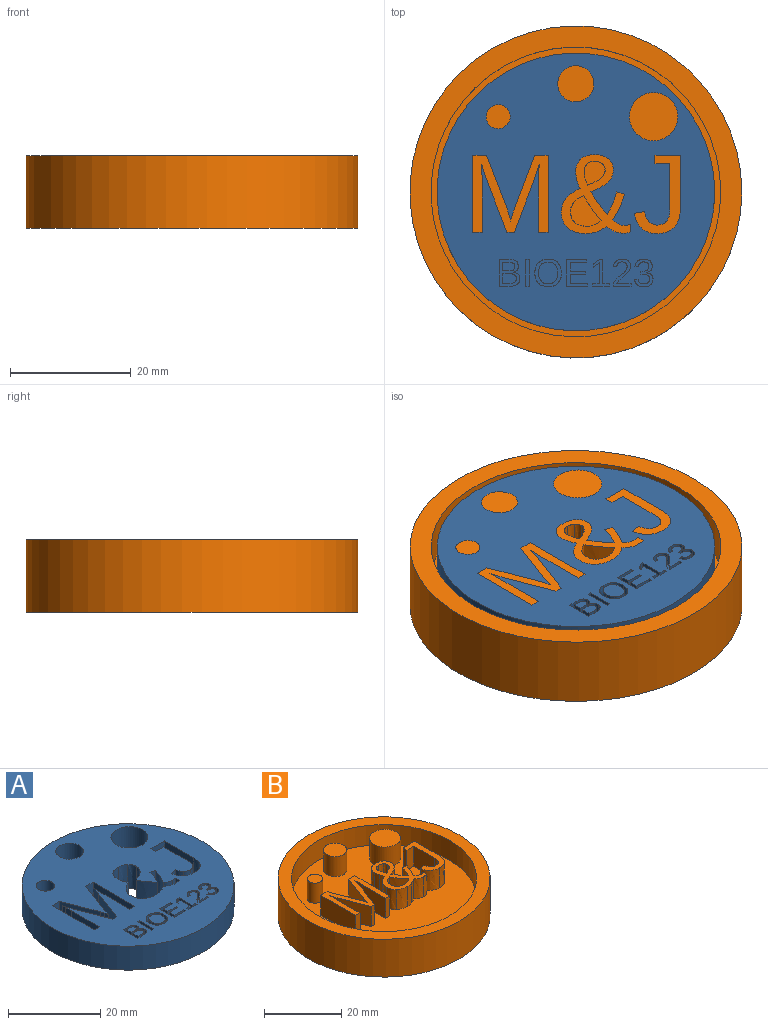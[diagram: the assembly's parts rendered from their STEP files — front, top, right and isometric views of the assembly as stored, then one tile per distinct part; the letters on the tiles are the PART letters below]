
ASSEMBLY  parts=2 mates=1
PART A: 196 faces, bbox 46x46x6.4 mm
  f0: plane 46x46mm, normal (0,0,1), area 1324.2mm2, adj f1,f2,f3,f4,f5,f6,f7,f8
  f1: plane 6.35x1.56mm, normal (0,1,0), area 9.9mm2, adj f0,f2,f62,f63
  f2: plane 8.56x6.35mm, normal (1,0,0), area 54.4mm2, adj f0,f1,f3,f63
  f3: extruded ~6.35x2.73mm, area 17.3mm2, adj f0,f2,f4,f63
  f4: extruded ~6.35x2.55mm, area 17mm2, adj f0,f3,f5,f63
  f5: plane 8.74x6.35mm, normal (-0.93,0.35,0), area 59.4mm2, adj f0,f4,f6,f63
  f6: plane 6.35x1.22mm, normal (0,1,0), area 7.7mm2, adj f0,f5,f7,f63
  f7: plane 8.74x6.35mm, normal (0.93,0.36,0), area 59.5mm2, adj f0,f6,f8,f63
  f8: plane 6.35x1.55mm, normal (0.95,0.31,0), area 10.3mm2, adj f0,f7,f9,f63
  f9: plane 6.35x1mm, normal (0.96,0.29,0), area 6.6mm2, adj f0,f8,f10,f63
  f10: plane 6.35x1.01mm, normal (-1,-0.03,0), area 6.4mm2, adj f0,f9,f11,f63
  f11: plane 6.35x1.72mm, normal (-1,-0.02,0), area 10.9mm2, adj f0,f10,f12,f63
  f12: plane 8.56x6.35mm, normal (-1,0,0), area 54.4mm2, adj f0,f11,f13,f63
  f13: plane 6.35x1.55mm, normal (0,1,0), area 9.8mm2, adj f0,f12,f14,f63
  f14: plane 12.83x6.35mm, normal (1,0,0), area 81.5mm2, adj f0,f13,f15,f63
  f15: plane 6.35x2.28mm, normal (0,-1,0), area 14.5mm2, adj f0,f14,f16,f63
  f16: plane 8.9x6.35mm, normal (-0.93,-0.36,0), area 60.5mm2, adj f0,f15,f17,f63
  f17: extruded ~6.35x1.15mm, area 7.6mm2, adj f0,f16,f18,f63
  f18: extruded ~6.35x0.89mm, area 5.8mm2, adj f0,f17,f19,f63
  f19: extruded ~6.35x1.11mm, area 7.3mm2, adj f0,f18,f20,f63
  f20: extruded ~6.35x0.93mm, area 6.3mm2, adj f0,f19,f21,f63
  f21: plane 8.9x6.35mm, normal (0.94,-0.35,0), area 60.4mm2, adj f0,f20,f22,f63
  f22: plane 6.35x2.23mm, normal (0,-1,0), area 14.2mm2, adj f0,f21,f62,f63
  f23: extruded ~6.35x1.29mm, area 8.3mm2, adj f0,f24,f56,f63
  f24: extruded ~6.35x2.71mm, area 19.3mm2, adj f0,f23,f25,f63
  f25: extruded ~6.35x1.56mm, area 11.5mm2, adj f0,f24,f26,f63
  f26: extruded ~6.35x1.83mm, area 11.9mm2, adj f0,f25,f27,f63
  f27: extruded ~6.35x3.03mm, area 20.6mm2, adj f0,f26,f28,f63
  f28: extruded ~6.35x2.62mm, area 18.6mm2, adj f0,f27,f29,f63
  f29: extruded ~6.35x3.91mm, area 33.8mm2, adj f0,f28,f30,f63
  f30: extruded ~6.35x1.34mm, area 9.1mm2, adj f0,f29,f31,f63
  f31: extruded ~6.35x1.41mm, area 9.1mm2, adj f0,f30,f32,f63
  f32: extruded ~6.35x2.12mm, area 14.9mm2, adj f0,f31,f33,f63
  f33: extruded ~6.35x2.36mm, area 16.1mm2, adj f0,f32,f34,f63
  f34: extruded ~6.35x2.22mm, area 15.1mm2, adj f0,f33,f35,f63
  f35: extruded ~6.35x1.89mm, area 13.6mm2, adj f0,f34,f36,f63
  f36: extruded ~6.35x1.91mm, area 13.6mm2, adj f0,f35,f37,f63
  f37: extruded ~6.35x2.89mm, area 21.3mm2, adj f0,f36,f38,f63
  f38: extruded ~6.35x3.75mm, area 29.3mm2, adj f0,f37,f39,f63
  f39: extruded ~6.35x3.73mm, area 25.8mm2, adj f0,f38,f40,f63
  f40: plane 6.35x1.32mm, normal (-0.28,-0.96,0), area 8.7mm2, adj f0,f39,f41,f63
  f41: extruded ~6.35x4.27mm, area 29.9mm2, adj f0,f40,f42,f63
  f42: extruded ~6.35x1.89mm, area 13.7mm2, adj f0,f41,f43,f63
  f43: extruded ~6.35x1.07mm, area 6.9mm2, adj f0,f42,f56,f63
  f44: extruded ~6.35x2.77mm, area 19.4mm2, adj f0,f45,f61,f63
  f45: extruded ~6.35x3.87mm, area 36.1mm2, adj f0,f44,f46,f63
  f46: plane 6.35x1.7mm, normal (0.16,-0.99,0), area 11mm2, adj f0,f45,f47,f63
  f47: extruded ~6.35x1.65mm, area 11.7mm2, adj f0,f46,f48,f63
  f48: extruded ~6.35x1.44mm, area 10.2mm2, adj f0,f47,f49,f63
  f49: extruded ~6.35x1.49mm, area 10.7mm2, adj f0,f48,f50,f63
  f50: extruded ~6.35x1.91mm, area 12.9mm2, adj f0,f49,f51,f63
  f51: plane 7.62x6.35mm, normal (1,0,0), area 48.4mm2, adj f0,f50,f52,f63
  f52: plane 6.35x2.47mm, normal (0,1,0), area 15.7mm2, adj f0,f51,f53,f63
  f53: plane 6.35x1.42mm, normal (1,0,0), area 9mm2, adj f0,f52,f54,f63
  f54: plane 6.35x4.2mm, normal (0,-1,0), area 26.7mm2, adj f0,f53,f55,f63
  f55: plane 9x6.35mm, normal (-1,0,0), area 57.2mm2, adj f0,f54,f61,f63
  f56: plane 6.35x1.23mm, normal (-1,0,0), area 7.8mm2, adj f0,f23,f43,f63
  f57: cylinder r=3mm len=6.35mm, axis (0,0,-1), area 119.7mm2, adj f0,f63
  f58: cylinder r=4mm len=8mm, axis (0,0,-1), area 159.6mm2, adj f0,f63
  f59: cylinder r=2mm len=6.35mm, axis (0,0,-1), area 79.8mm2, adj f0,f63
  f60: cylinder r=23mm len=46mm, axis (0,0,-1), area 917.7mm2, adj f0,f63
  f61: extruded ~6.35x2.94mm, area 20.2mm2, adj f0,f44,f55,f63
  f62: plane 12.83x6.35mm, normal (-1,0,0), area 81.5mm2, adj f0,f1,f22,f63
  f63: plane 46x46mm, normal (0,0,-1), area 1378.5mm2, adj f1,f2,f3,f4,f5,f6,f7,f8
  f64: plane 4.46x2mm, normal (1,0,0), area 8.9mm2, adj f0,f65,f67,f68
  f65: plane 2x0.6mm, normal (0,1,0), area 1.2mm2, adj f0,f64,f66,f68
  f66: plane 4.46x2mm, normal (-1,0,0), area 8.9mm2, adj f0,f65,f67,f68
  f67: plane 2x0.6mm, normal (0,-1,0), area 1.2mm2, adj f0,f64,f66,f68
  f68: plane 4.46x0.6mm, normal (0,0,1), area 2.7mm2, adj f64,f65,f66,f67
  f69: plane 4.46x2mm, normal (1,0,0), area 8.9mm2, adj f0,f70,f80,f81
  f70: plane 3.51x2mm, normal (0,1,0), area 7mm2, adj f0,f69,f71,f81
  f71: plane 2x0.49mm, normal (-1,0,0), area 1mm2, adj f0,f70,f72,f81
  f72: plane 2.91x2mm, normal (0,-1,0), area 5.8mm2, adj f0,f71,f73,f81
  f73: plane 2x1.55mm, normal (-1,0,0), area 3.1mm2, adj f0,f72,f74,f81
  f74: plane 2.59x2mm, normal (0,1,0), area 5.2mm2, adj f0,f73,f75,f81
  f75: plane 2x0.49mm, normal (-1,0,0), area 1mm2, adj f0,f74,f76,f81
  f76: plane 2.59x2mm, normal (0,-1,0), area 5.2mm2, adj f0,f75,f77,f81
  f77: plane 2x1.43mm, normal (-1,0,0), area 2.9mm2, adj f0,f76,f78,f81
  f78: plane 2.78x2mm, normal (0,1,0), area 5.6mm2, adj f0,f77,f79,f81
  f79: plane 2x0.49mm, normal (-1,0,0), area 1mm2, adj f0,f78,f80,f81
  f80: plane 3.38x2mm, normal (0,-1,0), area 6.8mm2, adj f0,f69,f79,f81
  f81: plane 4.46x3.51mm, normal (0,0,1), area 6.8mm2, adj f69,f70,f71,f72,f73,f74,f75,f76
  f82: plane 2x0.48mm, normal (1,0,0), area 1mm2, adj f0,f83,f92,f93
  f83: plane 2.79x2mm, normal (0,1,0), area 5.6mm2, adj f0,f82,f84,f93
  f84: plane 2x0.48mm, normal (-1,0,0), area 1mm2, adj f0,f83,f85,f93
  f85: plane 2x1.09mm, normal (0,-1,0), area 2.2mm2, adj f0,f84,f86,f93
  f86: plane 3.97x2mm, normal (-1,0,0), area 7.9mm2, adj f0,f85,f87,f93
  f87: plane 2x0.53mm, normal (0,-1,0), area 1.1mm2, adj f0,f86,f88,f93
  f88: plane 2x1.05mm, normal (0.57,-0.82,0), area 2.6mm2, adj f0,f87,f89,f93
  f89: plane 2x0.54mm, normal (1,0,0), area 1.1mm2, adj f0,f88,f90,f93
  f90: plane 2x1.01mm, normal (-0.58,0.81,0), area 2.5mm2, adj f0,f89,f91,f93
  f91: plane 3.43x2mm, normal (1,0,0), area 6.9mm2, adj f0,f90,f92,f93
  f92: plane 2x1.14mm, normal (0,-1,0), area 2.3mm2, adj f0,f82,f91,f93
  f93: plane 4.46x2.79mm, normal (0,0,1), area 4.2mm2, adj f82,f83,f84,f85,f86,f87,f88,f89
  f94: plane 2x0.4mm, normal (1,0,0), area 0.8mm2, adj f0,f95,f117,f118
  f95: plane 2.95x2mm, normal (0,1,0), area 5.9mm2, adj f0,f94,f96,f118
  f96: plane 2x0.48mm, normal (-1,0,0), area 1mm2, adj f0,f95,f97,f118
  f97: plane 2.33x2mm, normal (0,-1,0), area 4.7mm2, adj f0,f96,f98,f118
  f98: extruded ~2x0.46mm, area 1.1mm2, adj f0,f97,f99,f118
  f99: extruded ~2x0.58mm, area 1.6mm2, adj f0,f98,f100,f118
  f100: extruded ~2x0.9mm, area 2.4mm2, adj f0,f99,f101,f118
  f101: extruded ~2x0.51mm, area 1.2mm2, adj f0,f100,f102,f118
  f102: extruded ~2x0.52mm, area 1.1mm2, adj f0,f101,f103,f118
  f103: extruded ~2x0.9mm, area 2mm2, adj f0,f102,f104,f118
  f104: extruded ~2x1.04mm, area 2.2mm2, adj f0,f103,f105,f118
  f105: extruded ~2x1.01mm, area 2.2mm2, adj f0,f104,f106,f118
  f106: extruded ~2x0.85mm, area 2mm2, adj f0,f105,f107,f118
  f107: plane 2x0.58mm, normal (0.09,1,0), area 1.2mm2, adj f0,f106,f108,f118
  f108: extruded ~2x0.56mm, area 1.3mm2, adj f0,f107,f109,f118
  f109: extruded ~2x0.6mm, area 1.3mm2, adj f0,f108,f110,f118
  f110: extruded ~2x0.6mm, area 1.3mm2, adj f0,f109,f111,f118
  f111: extruded ~2x0.57mm, area 1.3mm2, adj f0,f110,f112,f118
  f112: extruded ~2x0.49mm, area 1mm2, adj f0,f111,f113,f118
  f113: extruded ~2x0.41mm, area 1.1mm2, adj f0,f112,f114,f118
  f114: extruded ~2x0.45mm, area 1.2mm2, adj f0,f113,f115,f118
  f115: extruded ~2x0.51mm, area 1.3mm2, adj f0,f114,f116,f118
  f116: extruded ~2x0.51mm, area 1.4mm2, adj f0,f115,f117,f118
  f117: extruded ~2x0.65mm, area 1.5mm2, adj f0,f94,f116,f118
  f118: plane 4.53x2.95mm, normal (0,0,1), area 5.1mm2, adj f94,f95,f96,f97,f98,f99,f100,f101
  f119: extruded ~2x0.96mm, area 2.1mm2, adj f0,f120,f147,f148
  f120: extruded ~2x0.71mm, area 1.6mm2, adj f0,f119,f121,f148
  f121: extruded ~2x0.78mm, area 1.7mm2, adj f0,f120,f122,f148
  f122: plane 2x0.01mm, normal (-1,0,0), area 0mm2, adj f0,f121,f123,f148
  f123: extruded ~2x0.69mm, area 1.6mm2, adj f0,f122,f124,f148
  f124: extruded ~2x0.69mm, area 1.5mm2, adj f0,f123,f125,f148
  f125: extruded ~2x0.87mm, area 2mm2, adj f0,f124,f126,f148
  f126: extruded ~2x1.04mm, area 2.2mm2, adj f0,f125,f127,f148
  f127: extruded ~2x1mm, area 2.1mm2, adj f0,f126,f128,f148
  f128: extruded ~2x0.85mm, area 2mm2, adj f0,f127,f129,f148
  f129: plane 2x0.57mm, normal (0.08,1,0), area 1.1mm2, adj f0,f128,f130,f148
  f130: extruded ~2x0.54mm, area 1.2mm2, adj f0,f129,f131,f148
  f131: extruded ~2x0.61mm, area 1.3mm2, adj f0,f130,f132,f148
  f132: extruded ~2x0.63mm, area 1.4mm2, adj f0,f131,f133,f148
  f133: extruded ~2x0.56mm, area 1.2mm2, adj f0,f132,f134,f148
  f134: extruded ~2x0.57mm, area 1.3mm2, adj f0,f133,f135,f148
  f135: extruded ~2x0.73mm, area 1.5mm2, adj f0,f134,f136,f148
  f136: plane 2x0.31mm, normal (0,-1,0), area 0.6mm2, adj f0,f135,f137,f148
  f137: plane 2x0.49mm, normal (1,0,0), area 1mm2, adj f0,f136,f138,f148
  f138: plane 2x0.32mm, normal (0,1,0), area 0.6mm2, adj f0,f137,f139,f148
  f139: extruded ~2x0.81mm, area 1.7mm2, adj f0,f138,f140,f148
  f140: extruded ~2x0.57mm, area 1.3mm2, adj f0,f139,f141,f148
  f141: extruded ~2x0.63mm, area 1.4mm2, adj f0,f140,f142,f148
  f142: extruded ~2x0.68mm, area 1.4mm2, adj f0,f141,f143,f148
  f143: extruded ~2x0.97mm, area 2.8mm2, adj f0,f142,f144,f148
  f144: plane 2x0.59mm, normal (0.09,-1,0), area 1.2mm2, adj f0,f143,f145,f148
  f145: extruded ~2x0.9mm, area 2.1mm2, adj f0,f144,f146,f148
  f146: extruded ~2x1.08mm, area 2.3mm2, adj f0,f145,f147,f148
  f147: extruded ~2x1.12mm, area 2.4mm2, adj f0,f119,f146,f148
  f148: plane 4.59x3.07mm, normal (0,0,1), area 5.4mm2, adj f119,f120,f121,f122,f123,f124,f125,f126
  f149: extruded ~2x1.31mm, area 2.8mm2, adj f150,f167,f168,f194
  f150: extruded ~2x1.35mm, area 2.9mm2, adj f149,f151,f168,f194
  f151: extruded ~2x1.19mm, area 2.6mm2, adj f150,f152,f168,f194
  f152: extruded ~2x1.17mm, area 2.6mm2, adj f151,f153,f168,f194
  f153: extruded ~2x1.33mm, area 2.9mm2, adj f152,f154,f168,f194
  f154: extruded ~2x1.31mm, area 2.8mm2, adj f153,f155,f168,f194
  f155: extruded ~2x1.18mm, area 2.6mm2, adj f154,f167,f168,f194
  f156: extruded ~2x1.22mm, area 2.5mm2, adj f0,f157,f166,f168
  f157: extruded ~2x1.22mm, area 2.5mm2, adj f0,f156,f158,f168
  f158: extruded ~2x0.79mm, area 2.2mm2, adj f0,f157,f159,f168
  f159: extruded ~2x1.18mm, area 2.4mm2, adj f0,f158,f160,f168
  f160: extruded ~2x1.63mm, area 3.6mm2, adj f0,f159,f161,f168
  f161: extruded ~2x1.67mm, area 3.6mm2, adj f0,f160,f162,f168
  f162: extruded ~2x1.23mm, area 2.5mm2, adj f0,f161,f163,f168
  f163: extruded ~2x0.81mm, area 2.3mm2, adj f0,f162,f164,f168
  f164: extruded ~2x1.18mm, area 2.5mm2, adj f0,f163,f165,f168
  f165: extruded ~2x1.18mm, area 2.5mm2, adj f0,f164,f166,f168
  f166: extruded ~2x0.81mm, area 2.3mm2, adj f0,f156,f165,f168
  f167: extruded ~2x1.18mm, area 2.6mm2, adj f149,f155,f168,f194
  f168: plane 4.59x4.42mm, normal (0,0,1), area 7.1mm2, adj f149,f150,f151,f152,f153,f154,f155,f156
  f169: extruded ~2x1.11mm, area 3.1mm2, adj f170,f191,f192,f195
  f170: extruded ~2x0.61mm, area 1.4mm2, adj f169,f171,f192,f195
  f171: extruded ~2x0.81mm, area 1.7mm2, adj f170,f172,f192,f195
  f172: plane 2x1.17mm, normal (0,-1,0), area 2.3mm2, adj f171,f173,f192,f195
  f173: plane 2x1.61mm, normal (-1,0,0), area 3.2mm2, adj f172,f191,f192,f195
  f174: extruded ~2x0.52mm, area 1.2mm2, adj f175,f189,f192,f193
  f175: extruded ~2x0.56mm, area 1.3mm2, adj f174,f176,f192,f193
  f176: extruded ~2x0.72mm, area 1.5mm2, adj f175,f177,f192,f193
  f177: plane 2x1.02mm, normal (0,-1,0), area 2mm2, adj f176,f178,f192,f193
  f178: plane 2x1.41mm, normal (-1,0,0), area 2.8mm2, adj f177,f179,f192,f193
  f179: plane 2x1.02mm, normal (0,1,0), area 2mm2, adj f178,f189,f192,f193
  f180: extruded ~2x0.93mm, area 2.1mm2, adj f0,f181,f190,f192
  f181: extruded ~2x0.74mm, area 1.6mm2, adj f0,f180,f182,f192
  f182: extruded ~2x0.82mm, area 1.8mm2, adj f0,f181,f183,f192
  f183: extruded ~2x0.63mm, area 1.5mm2, adj f0,f182,f184,f192
  f184: extruded ~2x0.66mm, area 1.4mm2, adj f0,f183,f185,f192
  f185: extruded ~2x1.57mm, area 4.3mm2, adj f0,f184,f186,f192
  f186: plane 2x1.62mm, normal (0,-1,0), area 3.2mm2, adj f0,f185,f187,f192
  f187: plane 4.46x2mm, normal (1,0,0), area 8.9mm2, adj f0,f186,f188,f192
  f188: plane 2x1.81mm, normal (0,1,0), area 3.6mm2, adj f0,f187,f190,f192
  f189: extruded ~2x0.72mm, area 1.5mm2, adj f174,f179,f192,f193
  f190: extruded ~2x1.21mm, area 2.5mm2, adj f0,f180,f188,f192
  f191: plane 2x1.13mm, normal (0,1,0), area 2.3mm2, adj f169,f173,f192,f195
  f192: plane 4.46x3.45mm, normal (0,0,1), area 7.8mm2, adj f169,f170,f171,f172,f173,f174,f175,f176
  f193: plane 1.98x1.41mm, normal (0,0,1), area 2.6mm2, adj f174,f175,f176,f177,f178,f179,f189
  f194: plane 3.6x3.19mm, normal (0,0,1), area 9.4mm2, adj f149,f150,f151,f152,f153,f154,f155,f167
  f195: plane 2.23x1.61mm, normal (0,0,1), area 3.3mm2, adj f169,f170,f171,f172,f173,f191
PART B: 88 faces, bbox 55x55x12 mm
  f0: plane 48x48mm, normal (0,0,1), area 1526.2mm2, adj f4,f6,f7,f8,f9,f10,f11,f12
  f1: cylinder r=27.5mm len=55mm, axis (0,0,-1), area 2073.5mm2, adj f2,f3
  f2: plane 55x55mm, normal (0,0,1), area 566.3mm2, adj f1,f4
  f3: plane 55x55mm, normal (0,0,-1), area 2375.8mm2, adj f1
  f4: cylinder r=24mm len=48mm, axis (0,0,1), area 957.6mm2, adj f0,f2
  f5: plane 12.83x12.47mm, normal (0,0,1), area 74.4mm2, adj f6,f7,f8,f9,f10,f11,f12,f13
  f6: plane 6.35x1.56mm, normal (0,-1,0), area 9.9mm2, adj f0,f5,f7,f27
  f7: plane 12.83x6.35mm, normal (1,0,0), area 81.5mm2, adj f0,f5,f6,f8
  f8: plane 6.35x2.23mm, normal (0,1,0), area 14.2mm2, adj f0,f5,f7,f9
  f9: plane 8.9x6.35mm, normal (-0.94,0.35,0), area 60.4mm2, adj f0,f5,f8,f10
  f10: extruded ~6.35x0.93mm, area 6.3mm2, adj f0,f5,f9,f11
  f11: extruded ~6.35x1.11mm, area 7.3mm2, adj f0,f5,f10,f12
  f12: extruded ~6.35x0.89mm, area 5.8mm2, adj f0,f5,f11,f13
  f13: extruded ~6.35x1.15mm, area 7.6mm2, adj f0,f5,f12,f14
  f14: plane 8.9x6.35mm, normal (0.93,0.36,0), area 60.5mm2, adj f0,f5,f13,f15
  f15: plane 6.35x2.28mm, normal (0,1,0), area 14.5mm2, adj f0,f5,f14,f16
  f16: plane 12.83x6.35mm, normal (-1,0,0), area 81.5mm2, adj f0,f5,f15,f17
  f17: plane 6.35x1.55mm, normal (0,-1,0), area 9.8mm2, adj f0,f5,f16,f18
  f18: plane 8.56x6.35mm, normal (1,0,0), area 54.4mm2, adj f0,f5,f17,f19
  f19: plane 6.35x1.72mm, normal (1,0.02,0), area 10.9mm2, adj f0,f5,f18,f20
  f20: plane 6.35x1.01mm, normal (1,0.03,0), area 6.4mm2, adj f0,f5,f19,f21
  f21: plane 6.35x1mm, normal (-0.96,-0.29,0), area 6.6mm2, adj f0,f5,f20,f22
  f22: plane 6.35x1.55mm, normal (-0.95,-0.31,0), area 10.3mm2, adj f0,f5,f21,f23
  f23: plane 8.74x6.35mm, normal (-0.93,-0.36,0), area 59.5mm2, adj f0,f5,f22,f24
  f24: plane 6.35x1.22mm, normal (0,-1,0), area 7.7mm2, adj f0,f5,f23,f25
  f25: plane 8.74x6.35mm, normal (0.93,-0.35,0), area 59.4mm2, adj f0,f5,f24,f26
  f26: extruded ~6.35x2.55mm, area 17mm2, adj f0,f5,f25,f28
  f27: plane 8.56x6.35mm, normal (-1,0,0), area 54.4mm2, adj f0,f5,f6,f28
  f28: extruded ~6.35x2.73mm, area 17.3mm2, adj f0,f5,f26,f27
  f29: plane 13.09x11.49mm, normal (0,0,1), area 57.4mm2, adj f30,f31,f32,f33,f34,f35,f36,f37
  f30: extruded ~6.35x1.13mm, area 8.5mm2, adj f29,f31,f58,f67
  f31: extruded ~6.35x1.29mm, area 8.4mm2, adj f29,f30,f32,f67
  f32: extruded ~6.35x1.93mm, area 13.2mm2, adj f29,f31,f57,f67
  f33: extruded ~6.35x0.9mm, area 6.1mm2, adj f29,f34,f64,f66
  f34: extruded ~6.35x0.85mm, area 7.3mm2, adj f29,f33,f35,f66
  f35: extruded ~6.35x1.75mm, area 12.4mm2, adj f29,f34,f36,f66
  f36: extruded ~6.35x2.22mm, area 14.7mm2, adj f29,f35,f37,f66
  f37: extruded ~6.35x1.3mm, area 9mm2, adj f29,f36,f63,f66
  f38: extruded ~6.35x1.29mm, area 8.3mm2, adj f0,f29,f39,f61
  f39: plane 6.35x1.23mm, normal (1,0,0), area 7.8mm2, adj f0,f29,f38,f40
  f40: extruded ~6.35x1.07mm, area 6.9mm2, adj f0,f29,f39,f41
  f41: extruded ~6.35x1.89mm, area 13.7mm2, adj f0,f29,f40,f42
  f42: extruded ~6.35x4.27mm, area 29.9mm2, adj f0,f29,f41,f43
  f43: plane 6.35x1.32mm, normal (0.28,0.96,0), area 8.7mm2, adj f0,f29,f42,f44
  f44: extruded ~6.35x3.73mm, area 25.8mm2, adj f0,f29,f43,f45
  f45: extruded ~6.35x3.75mm, area 29.3mm2, adj f0,f29,f44,f46
  f46: extruded ~6.35x2.89mm, area 21.3mm2, adj f0,f29,f45,f47
  f47: extruded ~6.35x1.91mm, area 13.6mm2, adj f0,f29,f46,f48
  f48: extruded ~6.35x1.89mm, area 13.6mm2, adj f0,f29,f47,f49
  f49: extruded ~6.35x2.22mm, area 15.1mm2, adj f0,f29,f48,f50
  f50: extruded ~6.35x2.36mm, area 16.1mm2, adj f0,f29,f49,f51
  f51: extruded ~6.35x2.12mm, area 14.9mm2, adj f0,f29,f50,f52
  f52: extruded ~6.35x1.41mm, area 9.1mm2, adj f0,f29,f51,f53
  f53: extruded ~6.35x1.34mm, area 9.1mm2, adj f0,f29,f52,f54
  f54: extruded ~6.35x3.91mm, area 33.8mm2, adj f0,f29,f53,f55
  f55: extruded ~6.35x2.62mm, area 18.6mm2, adj f0,f29,f54,f56
  f56: extruded ~6.35x3.03mm, area 20.6mm2, adj f0,f29,f55,f60
  f57: extruded ~6.35x1.74mm, area 12.3mm2, adj f29,f32,f59,f67
  f58: extruded ~6.35x4.16mm, area 32.3mm2, adj f29,f30,f59,f67
  f59: extruded ~6.35x2.74mm, area 23.6mm2, adj f29,f57,f58,f67
  f60: extruded ~6.35x1.83mm, area 11.9mm2, adj f0,f29,f56,f62
  f61: extruded ~6.35x2.71mm, area 19.3mm2, adj f0,f29,f38,f62
  f62: extruded ~6.35x1.56mm, area 11.5mm2, adj f0,f29,f60,f61
  f63: extruded ~6.35x1.33mm, area 9.2mm2, adj f29,f37,f65,f66
  f64: extruded ~6.35x1.07mm, area 7.6mm2, adj f29,f33,f65,f66
  f65: extruded ~6.35x1.24mm, area 8.5mm2, adj f29,f63,f64,f66
  f66: plane 3.99x3.48mm, normal (0,0,1), area 10.2mm2, adj f33,f34,f35,f36,f37,f63,f64,f65
  f67: plane 5.13x5.05mm, normal (0,0,1), area 15.9mm2, adj f30,f31,f32,f57,f58,f59
  f68: plane 13.01x7.65mm, normal (0,0,1), area 34.4mm2, adj f69,f70,f71,f72,f73,f74,f75,f76
  f69: extruded ~6.35x2.77mm, area 19.4mm2, adj f0,f68,f70,f80
  f70: extruded ~6.35x2.94mm, area 20.2mm2, adj f0,f68,f69,f71
  f71: plane 9x6.35mm, normal (1,0,0), area 57.2mm2, adj f0,f68,f70,f72
  f72: plane 6.35x4.2mm, normal (0,1,0), area 26.7mm2, adj f0,f68,f71,f73
  f73: plane 6.35x1.42mm, normal (-1,0,0), area 9mm2, adj f0,f68,f72,f74
  f74: plane 6.35x2.47mm, normal (0,-1,0), area 15.7mm2, adj f0,f68,f73,f75
  f75: plane 7.62x6.35mm, normal (-1,0,0), area 48.4mm2, adj f0,f68,f74,f76
  f76: extruded ~6.35x1.91mm, area 12.9mm2, adj f0,f68,f75,f77
  f77: extruded ~6.35x1.49mm, area 10.7mm2, adj f0,f68,f76,f78
  f78: extruded ~6.35x1.44mm, area 10.2mm2, adj f0,f68,f77,f79
  f79: extruded ~6.35x1.65mm, area 11.7mm2, adj f0,f68,f78,f81
  f80: extruded ~6.35x3.87mm, area 36.1mm2, adj f0,f68,f69,f81
  f81: plane 6.35x1.7mm, normal (-0.16,0.99,0), area 11mm2, adj f0,f68,f79,f80
  f82: plane 6x6mm, normal (0,0,1), area 28.3mm2, adj f83
  f83: cylinder r=3mm len=6.35mm, axis (0,0,-1), area 119.7mm2, adj f0,f82
  f84: plane 8x8mm, normal (0,0,1), area 50.3mm2, adj f85
  f85: cylinder r=4mm len=8mm, axis (0,0,-1), area 159.6mm2, adj f0,f84
  f86: plane 4x4mm, normal (0,0,1), area 12.6mm2, adj f87
  f87: cylinder r=2mm len=6.35mm, axis (0,0,-1), area 79.8mm2, adj f0,f86
PLACE A t=(-9.65,2.18,-2.84)mm
PLACE B t=(-9.65,-5.35,-8.49)mm
MATE cylindrical B.f4 <-> A.f60  axis (0,0,1) through (-9.65,-5.35,0.34)mm
